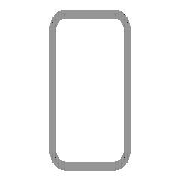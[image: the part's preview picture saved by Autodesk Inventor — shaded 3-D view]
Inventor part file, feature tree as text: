
AUTODESK INVENTOR PART (.ipt)
format: ipt  version: 2025 (Build 290162010, 162A)  size: 147,456 bytes
history: native  units: mm (DEFAULTED — no unit token found)
features: other x3, sketch x2, extrude x1, plane x1
ambient origin geometry x8: Origin, YZ Plane, XZ Plane, XY Plane, X Axis, Y Axis, Z Axis, Center Point
bodies: Solid1 (feature_tree), Body (feature_tree)
feature tree (7):
  other  "Driven Length"
  other  "Start plane"
  other  "End plane"
  extrude  "Extrusion2"  TaperAngle=0.0deg  [1 undecoded]
  sketch  "Sketch3"  dims[d3=1300.0mm d4=0.0mm]
  plane  "Work Plane3"
  sketch  "Sketch5"  dims[d7=4.0mm d9=40.0mm d11=80.0mm d12=2.0mm d13=-0.0mm d14=1300.0mm d15=20.0mm d16=40.0mm d17=90.0deg d18=1300.0mm d19=5.846853mm d20=0.0mm d21=0.0mm]
note: 1 required parameter value undecoded (feature->parameter linkage not recoverable at this tier; creation-order binding heuristic only, values carry confidence <= 0.55)
